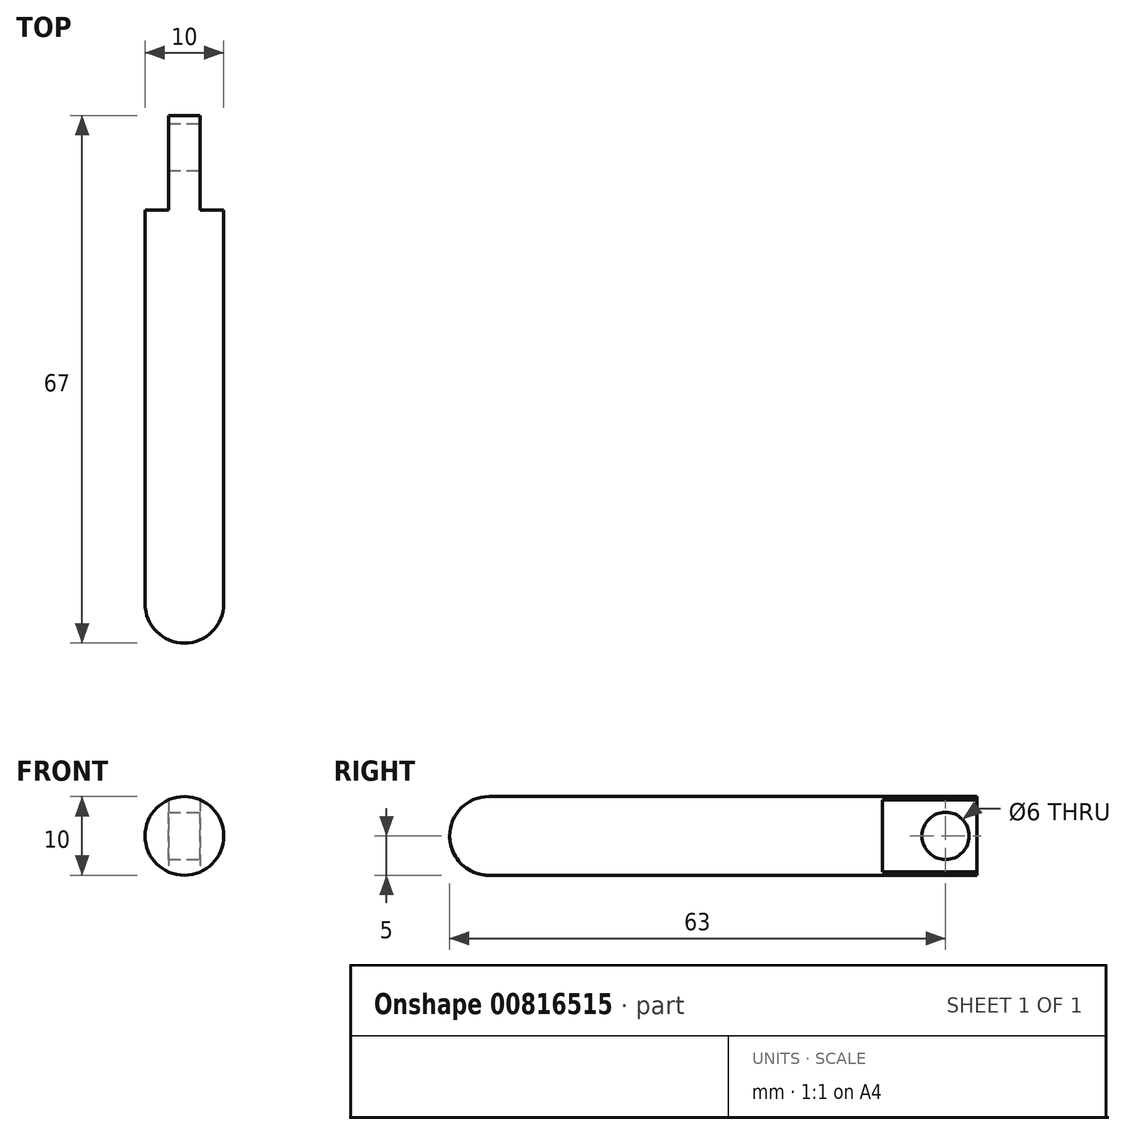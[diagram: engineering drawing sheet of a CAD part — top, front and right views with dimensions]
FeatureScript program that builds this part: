
annotation { "Feature Type Name" : "Feature", "Feature Type Description" : "" }
export const myFeature = defineFeature(function(context is Context, id is Id, definition is map)
    precondition{}
    {
        {
            assignVariable(context, id + "F0", {"name" : "Mlaenge", "anyValue" : 67});
        }
        {
            var Q0;
            Q0=qCreatedBy(makeId("Front.planeOp"),FACE);
            var sketch = newSketch(context, id + "F1", { "sketchPlane" : qUnion([Q0])});
            skCircle(sketch, "E0", {"center": v(0, 0) * mm, "radius": 5 * mm});
            skLineSegment(sketch, "E1", {"start": v(-2, 4.58) * mm, "end": v(-2, -4.58) * mm});
            skLineSegment(sketch, "E2.MirrorCS", {"start": v(2, 4.58) * mm, "end": v(2, -4.58) * mm});
            skPoint(sketch, "E3.orphan", {"position": v(-2, 6.45) * mm});
            skPoint(sketch, "E4.orphan", {"position": v(2, 6.45) * mm});
            skPoint(sketch, "E5.orphan", {"position": v(-2, -7.13) * mm});
            skPoint(sketch, "E6.orphan", {"position": v(2, -7.13) * mm});
            skSolve(sketch);
        }
        {
            var Q0;
            Q0 = qSketchRegion(id + "F1", true);
            extrude(context, id + "F2", {"entities" : qUnion([Q0]), "depth" : (getVariable(context, 'Mlaenge')) * mm, "offsetDistance" : 25 * mm});
        }
        {
            var Q0;
            {var subQ0=sQuery(id+"F1.wireOp",EDGE,"E1");Q0=makeQuery(id+"F1.imprint","IMPRINT",FACE,{"disambiguationData":[TD([[makeQuery(id+"F1.imprint","IMPRINT",EDGE,{"derivedFrom":subQ0}),-1.0]])]});}
            var Q1;
            {var subQ0=sQuery(id+"F1.wireOp",EDGE,"E2.MirrorCS");Q1=makeQuery(id+"F1.imprint","IMPRINT",FACE,{"disambiguationData":[TD([[makeQuery(id+"F1.imprint","IMPRINT",EDGE,{"derivedFrom":subQ0}),1.0]])]});}
            extrude(context, id + "F3", {"entities" : qUnion([Q0, Q1]), "operationType" : NewBodyOperationType.REMOVE, "depth" : 12 * mm, "offsetDistance" : 25 * mm});
        }
        {
            var Q0;
            Q0=makeQuery(id+"F3.boolean.opBoolean","COPY",FACE,{"derivedFrom":makeQuery(id+"F3.opExtrude","SWEPT_FACE",FACE,{"disambiguationData":[OSD([sQuery(id+"F1.wireOp",EDGE,"E2.MirrorCS")])]})});
            var sketch = newSketch(context, id + "F4", { "sketchPlane" : qUnion([Q0])});
            skCircle(sketch, "E7", {"center": v(-4, 0) * mm, "radius": 3 * mm});
            skSolve(sketch);
        }
        {
            var Q0;
            Q0=makeQuery(id+"F4.imprint","IMPRINT",FACE,{"disambiguationData":[TD([[makeQuery(id+"F4.imprint","IMPRINT",EDGE,{"derivedFrom":sQuery(id+"F4.wireOp",EDGE,"E7")}),1.0]])]});
            extrude(context, id + "F5", {"entities" : qUnion([Q0]), "operationType" : NewBodyOperationType.REMOVE, "oppositeDirection" : true, "depth" : 25 * mm, "offsetDistance" : 25 * mm});
        }
        {
            var Q0;
            Q0=makeQuery(id+"F2.opExtrude","CAP_EDGE",EDGE,{"disambiguationData":[OSD([sQuery(id+"F1.wireOp",EDGE,"E0")])],"isStart":false});
            fillet(context, id + "F6", {"entities" : qUnion([Q0]), "radius" : 5 * mm, "tangentPropagation" : true, "allowEdgeOverflow" : false});
        }
    });
